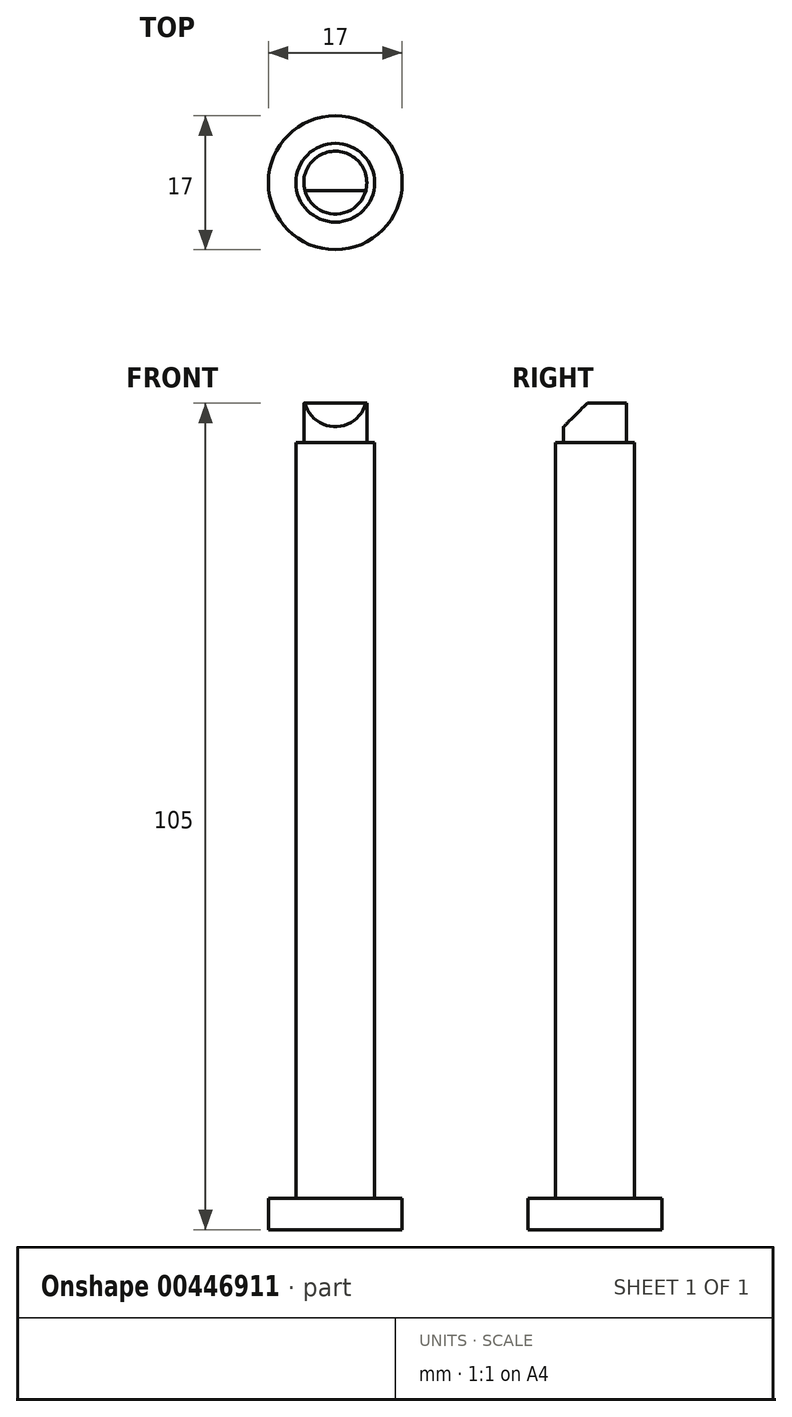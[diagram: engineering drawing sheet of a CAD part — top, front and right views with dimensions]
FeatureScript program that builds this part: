
annotation { "Feature Type Name" : "Feature", "Feature Type Description" : "" }
export const myFeature = defineFeature(function(context is Context, id is Id, definition is map)
    precondition{}
    {
        {
            var Q0;
            Q0=qCreatedBy(makeId("Top.planeOp"),FACE);
            var sketch = newSketch(context, id + "F0", { "sketchPlane" : qUnion([Q0])});
            skCircle(sketch, "E0", {"center": v(0, 0) * mm, "radius": 8.5 * mm});
            skSolve(sketch);
        }
        {
            var Q0;
            Q0=qSketchRegion(id+"F0",true);
            extrude(context, id + "F1", {"entities" : qUnion([Q0]), "depth" : 4 * mm});
        }
        {
            var Q0;
            Q0=qCreatedBy(makeId("Top.planeOp"),FACE);
            cPlane(context, id + "F2", {"entities" : qUnion([Q0]), "cplaneType" : CPlaneType.OFFSET, "offset" : 4 * mm, "width" : 150 * mm, "height" : 150 * mm});
        }
        {
            var Q0;
            Q0=qCreatedBy(makeId("Top.planeOp"),FACE);
            var sketch = newSketch(context, id + "F3", { "sketchPlane" : qUnion([Q0])});
            skCircle(sketch, "E1", {"center": v(0, 0) * mm, "radius": 5 * mm});
            skSolve(sketch);
        }
        {
            var Q0;
            Q0=qSketchRegion(id+"F3",true);
            extrude(context, id + "F4", {"entities" : qUnion([Q0]), "operationType" : NewBodyOperationType.ADD, "depth" : 100 * mm});
        }
        {
            var Q0;
            Q0=qCreatedBy(makeId("Right.planeOp"),FACE);
            var sketch = newSketch(context, id + "F5", { "sketchPlane" : qUnion([Q0])});
            skLineSegment(sketch, "E2.bottom", {"start": v(0, 105) * mm, "end": v(4, 105) * mm});
            skLineSegment(sketch, "E2.top", {"start": v(0, 100) * mm, "end": v(4, 100) * mm});
            skLineSegment(sketch, "E2.left", {"start": v(0, 105) * mm, "end": v(0, 100) * mm});
            skLineSegment(sketch, "E2.right", {"start": v(4, 105) * mm, "end": v(4, 100) * mm});
            skSolve(sketch);
        }
        {
            var Q0;
            Q0=makeQuery(id+"F5.imprint","IMPRINT",FACE,{"disambiguationData":[TD([[makeQuery(id+"F5.imprint","IMPRINT",EDGE,{"derivedFrom":sQuery(id+"F5.wireOp",EDGE,"E2.bottom")}),-1.0]])]});
            var Q1;
            Q1=sQuery(id+"F5.wireOp",EDGE,"E2.left");
            revolve(context, id + "F6", {"operationType" : NewBodyOperationType.ADD, "entities" : qUnion([Q0]), "axis" : qUnion([Q1]), "revolveType" : RevolveType.FULL});
        }
        {
            var Q0;
            Q0=qCreatedBy(id+"F2.planeOp",FACE);
            var sketch = newSketch(context, id + "F7", { "sketchPlane" : qUnion([Q0])});
            skLineSegment(sketch, "E3", {"start": v(8.44, 1) * mm, "end": v(8.44, -1) * mm});
            skSolve(sketch);
        }
        {
            var Q0;
            Q0=qCreatedBy(makeId("Right.planeOp"),FACE);
            var sketch = newSketch(context, id + "F8", { "sketchPlane" : qUnion([Q0])});
            skLineSegment(sketch, "E4", {"start": v(-5, 106) * mm, "end": v(0, 106) * mm});
            skLineSegment(sketch, "E5", {"start": v(0, 106) * mm, "end": v(-5, 101) * mm});
            skLineSegment(sketch, "E6", {"start": v(-5, 101) * mm, "end": v(-5, 106) * mm});
            skSolve(sketch);
        }
        {
            var Q0;
            Q0=makeQuery(id+"F8.imprint","IMPRINT",FACE,{"disambiguationData":[TD([[makeQuery(id+"F8.imprint","IMPRINT",EDGE,{"derivedFrom":sQuery(id+"F8.wireOp",EDGE,"E4")}),-1.0]])]});
            extrude(context, id + "F9", {"entities" : qUnion([Q0]), "operationType" : NewBodyOperationType.REMOVE, "endBound" : BoundingType.THROUGH_ALL, "oppositeDirection" : true, "depth" : 25 * mm, "hasSecondDirection" : true, "secondDirectionOppositeDirection" : false, "secondDirectionDepth" : 25 * mm});
        }
    });
